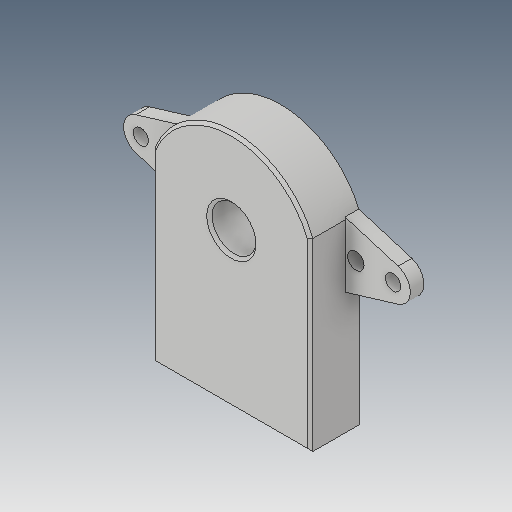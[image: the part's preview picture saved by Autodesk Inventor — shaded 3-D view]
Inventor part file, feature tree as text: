
AUTODESK INVENTOR PART (.ipt)
format: ipt  version: 2020.3 (Build 243373000, 373)  size: 160,256 bytes
history: native  units: mm
features: extrude x3, sketch x3, other x1, chamfer x1
ambient origin geometry x8: Origin, YZ Plane, XZ Plane, XY Plane, X Axis, Y Axis, Z Axis, Center Point
bodies: Body1 (feature_tree)
feature tree (8):
  other  "ソリッド1"
  extrude  "押し出し1"  Depth=15.5mm
  extrude  "押し出し3"  Depth=43.38mm
  extrude  "押し出し4"  Depth=15.34mm
  chamfer  "面取り1"  Distance=8.0mm
  sketch  "スケッチ1"
  sketch  "スケッチ4"
  sketch  "スケッチ5"
